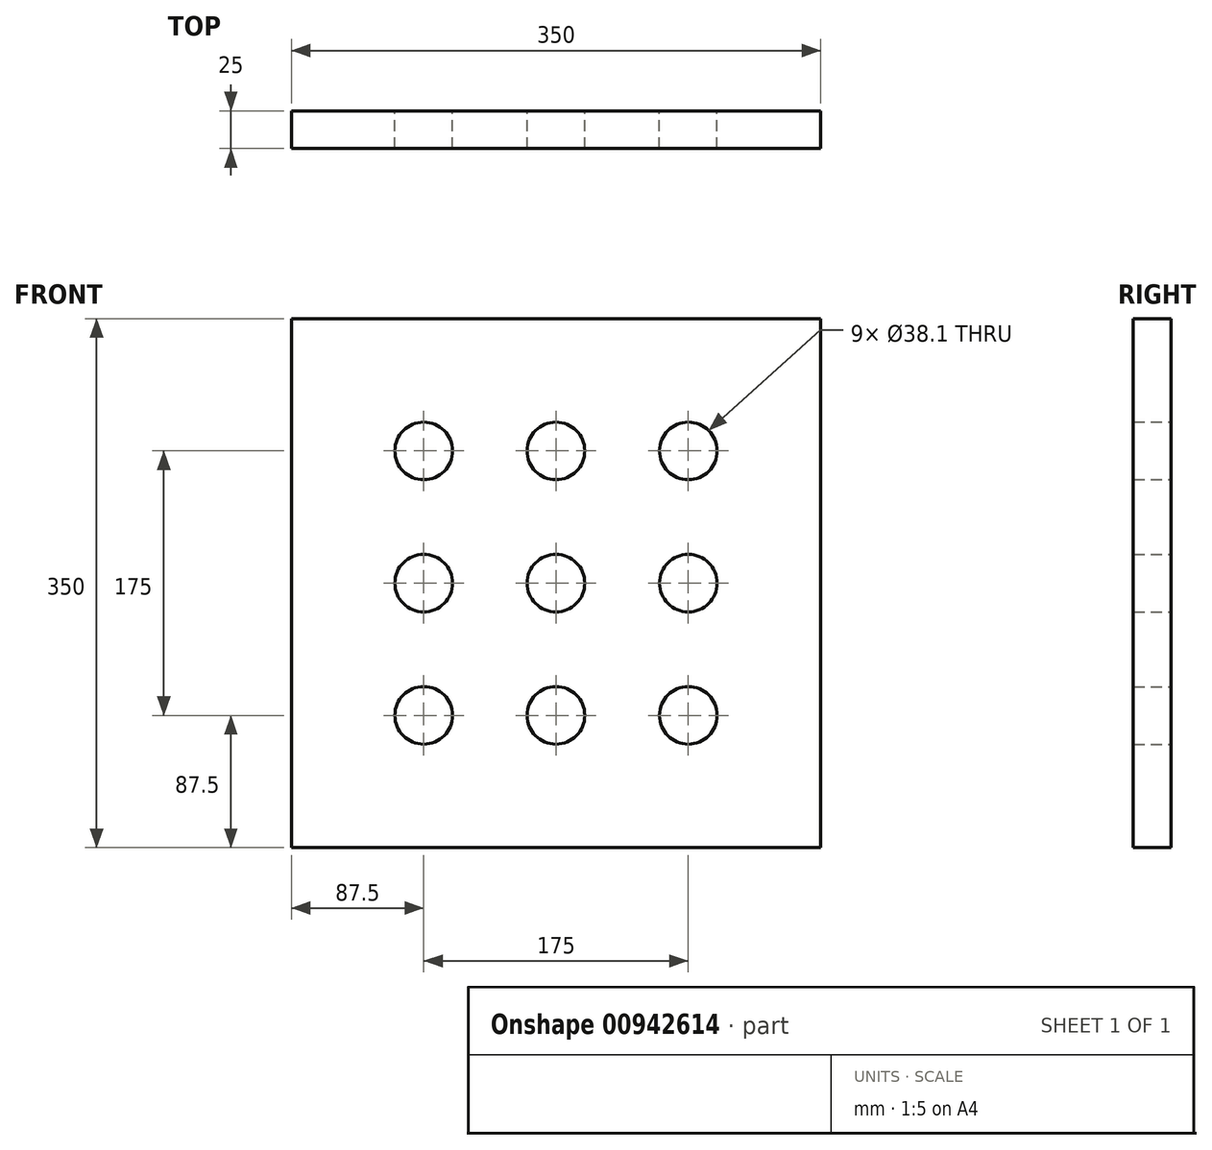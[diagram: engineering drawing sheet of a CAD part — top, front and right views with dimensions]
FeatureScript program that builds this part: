
annotation { "Feature Type Name" : "Feature", "Feature Type Description" : "" }
export const myFeature = defineFeature(function(context is Context, id is Id, definition is map)
    precondition{}
    {
        {
            var Q0;
            Q0=qCreatedBy(makeId("Front.planeOp"),FACE);
            var sketch = newSketch(context, id + "F0", { "sketchPlane" : qUnion([Q0])});
            skLineSegment(sketch, "E0.bottom", {"start": v(-175, 175) * mm, "end": v(175, 175) * mm});
            skLineSegment(sketch, "E0.top", {"start": v(-175, -175) * mm, "end": v(175, -175) * mm});
            skLineSegment(sketch, "E0.left", {"start": v(-175, 175) * mm, "end": v(-175, -175) * mm});
            skLineSegment(sketch, "E0.right", {"start": v(175, 175) * mm, "end": v(175, -175) * mm});
            skLineSegment(sketch, "E1", {"start": v(-87.5, 175) * mm, "end": v(-87.5, -175) * mm, "construction": true});
            skLineSegment(sketch, "E2", {"start": v(0, 175) * mm, "end": v(0, -175) * mm, "construction": true});
            skPoint(sketch, "E2.endSnap0", {"position": v(0, -175) * mm});
            skLineSegment(sketch, "E3", {"start": v(87.5, 175) * mm, "end": v(87.5, -175) * mm, "construction": true});
            skLineSegment(sketch, "E4", {"start": v(-175, 87.5) * mm, "end": v(175, 87.5) * mm, "construction": true});
            skLineSegment(sketch, "E5", {"start": v(-175, 0) * mm, "end": v(175, 0) * mm, "construction": true});
            skLineSegment(sketch, "E6", {"start": v(-175, -87.5) * mm, "end": v(175, -87.5) * mm, "construction": true});
            skCircle(sketch, "E7", {"center": v(-87.5, 87.5) * mm, "radius": 19.05 * mm});
            skCircle(sketch, "E8.0.1.0", {"center": v(-87.5, 0) * mm, "radius": 19.05 * mm});
            skCircle(sketch, "E8.0.2.0", {"center": v(-87.5, -87.5) * mm, "radius": 19.05 * mm});
            skCircle(sketch, "E8.1.0.0", {"center": v(0, 87.5) * mm, "radius": 19.05 * mm});
            skCircle(sketch, "E8.1.1.0", {"center": v(0, 0) * mm, "radius": 19.05 * mm});
            skCircle(sketch, "E8.1.2.0", {"center": v(0, -87.5) * mm, "radius": 19.05 * mm});
            skCircle(sketch, "E8.2.0.0", {"center": v(87.5, 87.5) * mm, "radius": 19.05 * mm});
            skCircle(sketch, "E8.2.1.0", {"center": v(87.5, 0) * mm, "radius": 19.05 * mm});
            skCircle(sketch, "E8.2.2.0", {"center": v(87.5, -87.5) * mm, "radius": 19.05 * mm});
            skLineSegment(sketch, "E8.direction1", {"start": v(-87.5, 87.5) * mm, "end": v(0, 87.5) * mm, "construction": true});
            skLineSegment(sketch, "E8.direction2", {"start": v(-87.5, 87.5) * mm, "end": v(-87.5, 0) * mm, "construction": true});
            skSolve(sketch);
        }
        {
            var Q0;
            Q0 = qSketchRegion(id + "F0", true);
            extrude(context, id + "F1", {"entities" : qUnion([Q0]), "depth" : 25 * mm, "offsetDistance" : 25 * mm});
        }
    });
